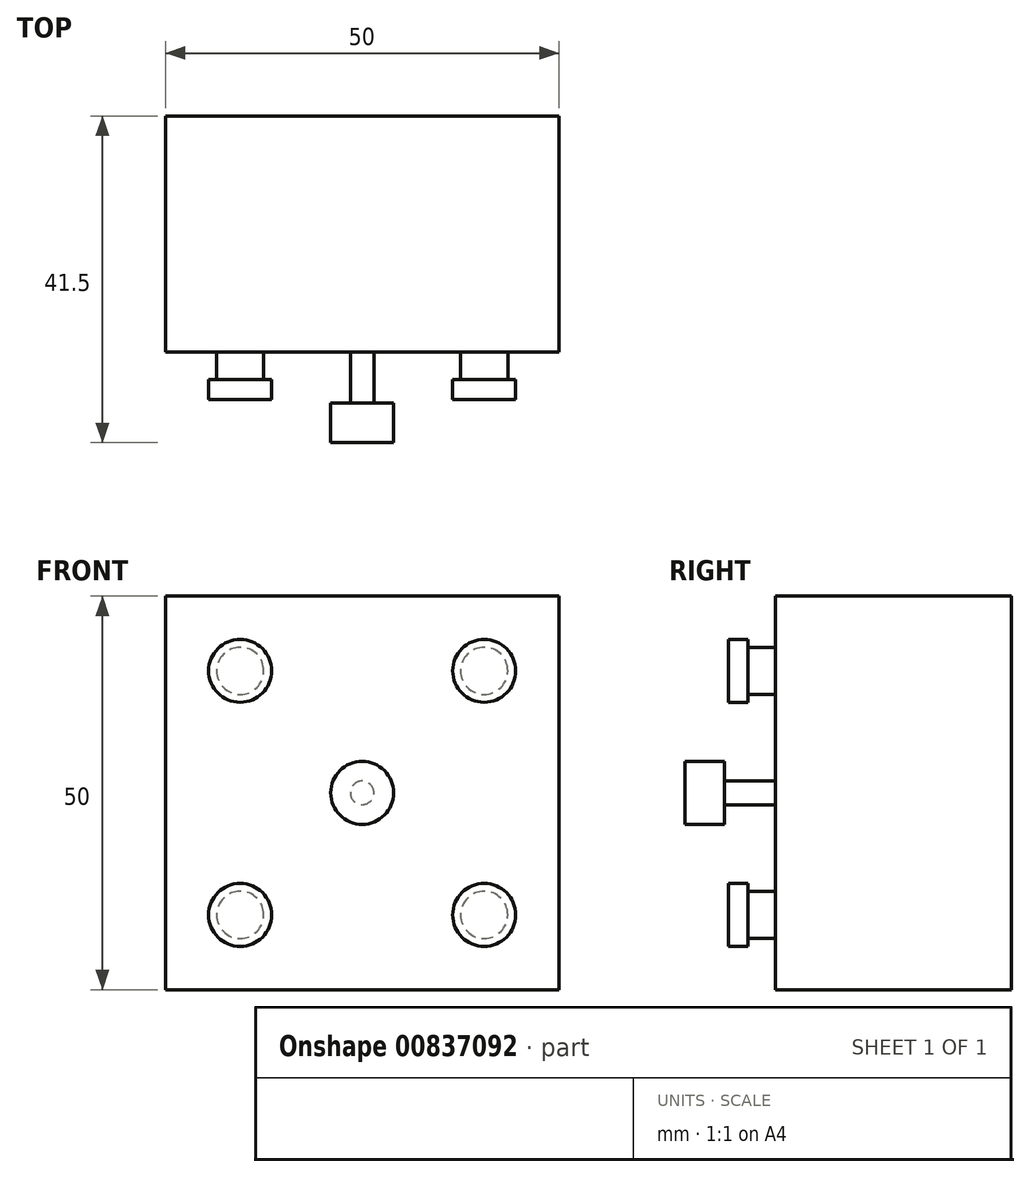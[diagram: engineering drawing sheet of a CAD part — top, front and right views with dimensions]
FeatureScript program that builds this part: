
annotation { "Feature Type Name" : "Feature", "Feature Type Description" : "" }
export const myFeature = defineFeature(function(context is Context, id is Id, definition is map)
    precondition{}
    {
        {
            var Q0;
            Q0=qCreatedBy(makeId("Front.planeOp"),FACE);
            var sketch = newSketch(context, id + "F0", { "sketchPlane" : qUnion([Q0])});
            skLineSegment(sketch, "E0.bottom", {"start": v(-25, 25) * mm, "end": v(25, 25) * mm});
            skLineSegment(sketch, "E0.top", {"start": v(-25, -25) * mm, "end": v(25, -25) * mm});
            skLineSegment(sketch, "E0.left", {"start": v(-25, 25) * mm, "end": v(-25, -25) * mm});
            skLineSegment(sketch, "E0.right", {"start": v(25, 25) * mm, "end": v(25, -25) * mm});
            skPoint(sketch, "E0.middle", {"position": v(0, 0) * mm});
            skCircle(sketch, "E1", {"center": v(-15.5, 15.5) * mm, "radius": 4 * mm});
            skCircle(sketch, "E2", {"center": v(15.5, 15.5) * mm, "radius": 4 * mm});
            skCircle(sketch, "E3", {"center": v(-15.5, -15.5) * mm, "radius": 4 * mm});
            skCircle(sketch, "E4", {"center": v(15.5, -15.5) * mm, "radius": 4 * mm});
            skCircle(sketch, "E5", {"center": v(-15.5, 15.5) * mm, "radius": 3 * mm});
            skCircle(sketch, "E6", {"center": v(15.5, 15.5) * mm, "radius": 3 * mm});
            skCircle(sketch, "E7", {"center": v(-15.5, -15.5) * mm, "radius": 3 * mm});
            skCircle(sketch, "E8", {"center": v(15.5, -15.5) * mm, "radius": 3 * mm});
            skLineSegment(sketch, "E9", {"start": v(25, 25) * mm, "end": v(-25, -25) * mm, "construction": true});
            skLineSegment(sketch, "E10", {"start": v(-25, 25) * mm, "end": v(25, -25) * mm, "construction": true});
            skCircle(sketch, "E11", {"center": v(0, 0) * mm, "radius": 4 * mm});
            skCircle(sketch, "E12", {"center": v(0, 0) * mm, "radius": 1.5 * mm});
            skSolve(sketch);
        }
        {
            var Q0;
            Q0=makeQuery(id+"F0.imprint","IMPRINT",FACE,{"disambiguationData":[TD([[makeQuery(id+"F0.imprint","IMPRINT",EDGE,{"derivedFrom":sQuery(id+"F0.wireOp",EDGE,"E0.bottom")}),-1.0]])]});
            var Q1;
            Q1=makeQuery(id+"F0.imprint","IMPRINT",FACE,{"disambiguationData":[TD([[makeQuery(id+"F0.imprint","IMPRINT",EDGE,{"derivedFrom":sQuery(id+"F0.wireOp",EDGE,"E1")}),1.0]])]});
            var Q2;
            Q2=makeQuery(id+"F0.imprint","IMPRINT",FACE,{"disambiguationData":[TD([[makeQuery(id+"F0.imprint","IMPRINT",EDGE,{"derivedFrom":sQuery(id+"F0.wireOp",EDGE,"E3")}),1.0]])]});
            var Q3;
            Q3=makeQuery(id+"F0.imprint","IMPRINT",FACE,{"disambiguationData":[TD([[makeQuery(id+"F0.imprint","IMPRINT",EDGE,{"derivedFrom":sQuery(id+"F0.wireOp",EDGE,"E4")}),1.0]])]});
            var Q4;
            Q4=makeQuery(id+"F0.imprint","IMPRINT",FACE,{"disambiguationData":[TD([[makeQuery(id+"F0.imprint","IMPRINT",EDGE,{"derivedFrom":sQuery(id+"F0.wireOp",EDGE,"E2")}),1.0]])]});
            var Q5;
            Q5=makeQuery(id+"F0.imprint","IMPRINT",FACE,{"disambiguationData":[TD([[makeQuery(id+"F0.imprint","IMPRINT",EDGE,{"derivedFrom":sQuery(id+"F0.wireOp",EDGE,"E8")}),1.0]])]});
            var Q6;
            Q6=makeQuery(id+"F0.imprint","IMPRINT",FACE,{"disambiguationData":[TD([[makeQuery(id+"F0.imprint","IMPRINT",EDGE,{"derivedFrom":sQuery(id+"F0.wireOp",EDGE,"E7")}),1.0]])]});
            var Q7;
            Q7=makeQuery(id+"F0.imprint","IMPRINT",FACE,{"disambiguationData":[TD([[makeQuery(id+"F0.imprint","IMPRINT",EDGE,{"derivedFrom":sQuery(id+"F0.wireOp",EDGE,"E6")}),1.0]])]});
            var Q8;
            Q8=makeQuery(id+"F0.imprint","IMPRINT",FACE,{"disambiguationData":[TD([[makeQuery(id+"F0.imprint","IMPRINT",EDGE,{"derivedFrom":sQuery(id+"F0.wireOp",EDGE,"E5")}),1.0]])]});
            var Q9;
            Q9=makeQuery(id+"F0.imprint","IMPRINT",FACE,{"disambiguationData":[TD([[makeQuery(id+"F0.imprint","IMPRINT",EDGE,{"derivedFrom":sQuery(id+"F0.wireOp",EDGE,"E11")}),1.0]])]});
            var Q10;
            Q10=makeQuery(id+"F0.imprint","IMPRINT",FACE,{"disambiguationData":[TD([[makeQuery(id+"F0.imprint","IMPRINT",EDGE,{"derivedFrom":sQuery(id+"F0.wireOp",EDGE,"E12")}),1.0]])]});
            extrude(context, id + "F1", {"entities" : qUnion([Q0, Q1, Q2, Q3, Q4, Q5, Q6, Q7, Q8, Q9, Q10]), "oppositeDirection" : true, "depth" : 30 * mm, "offsetDistance" : 25 * mm});
        }
        {
            var Q0;
            Q0=makeQuery(id+"F0.imprint","IMPRINT",FACE,{"disambiguationData":[TD([[makeQuery(id+"F0.imprint","IMPRINT",EDGE,{"derivedFrom":sQuery(id+"F0.wireOp",EDGE,"E1")}),1.0]])]});
            var Q1;
            Q1=makeQuery(id+"F0.imprint","IMPRINT",FACE,{"disambiguationData":[TD([[makeQuery(id+"F0.imprint","IMPRINT",EDGE,{"derivedFrom":sQuery(id+"F0.wireOp",EDGE,"E2")}),1.0]])]});
            var Q2;
            Q2=makeQuery(id+"F0.imprint","IMPRINT",FACE,{"disambiguationData":[TD([[makeQuery(id+"F0.imprint","IMPRINT",EDGE,{"derivedFrom":sQuery(id+"F0.wireOp",EDGE,"E4")}),1.0]])]});
            var Q3;
            Q3=makeQuery(id+"F0.imprint","IMPRINT",FACE,{"disambiguationData":[TD([[makeQuery(id+"F0.imprint","IMPRINT",EDGE,{"derivedFrom":sQuery(id+"F0.wireOp",EDGE,"E3")}),1.0]])]});
            extrude(context, id + "F2", {"entities" : qUnion([Q0, Q1, Q2, Q3]), "operationType" : NewBodyOperationType.ADD, "depth" : 6 * mm, "offsetDistance" : 25 * mm});
        }
        {
            var Q0;
            Q0=makeQuery(id+"F0.imprint","IMPRINT",FACE,{"disambiguationData":[TD([[makeQuery(id+"F0.imprint","IMPRINT",EDGE,{"derivedFrom":sQuery(id+"F0.wireOp",EDGE,"E5")}),1.0]])]});
            var Q1;
            Q1=makeQuery(id+"F0.imprint","IMPRINT",FACE,{"disambiguationData":[TD([[makeQuery(id+"F0.imprint","IMPRINT",EDGE,{"derivedFrom":sQuery(id+"F0.wireOp",EDGE,"E6")}),1.0]])]});
            var Q2;
            Q2=makeQuery(id+"F0.imprint","IMPRINT",FACE,{"disambiguationData":[TD([[makeQuery(id+"F0.imprint","IMPRINT",EDGE,{"derivedFrom":sQuery(id+"F0.wireOp",EDGE,"E8")}),1.0]])]});
            var Q3;
            Q3=makeQuery(id+"F0.imprint","IMPRINT",FACE,{"disambiguationData":[TD([[makeQuery(id+"F0.imprint","IMPRINT",EDGE,{"derivedFrom":sQuery(id+"F0.wireOp",EDGE,"E7")}),1.0]])]});
            extrude(context, id + "F3", {"entities" : qUnion([Q0, Q1, Q2, Q3]), "operationType" : NewBodyOperationType.ADD, "depth" : 6 * mm, "offsetDistance" : 25 * mm});
        }
        {
            var Q0;
            Q0=makeQuery(id+"F0.imprint","IMPRINT",FACE,{"disambiguationData":[TD([[makeQuery(id+"F0.imprint","IMPRINT",EDGE,{"derivedFrom":sQuery(id+"F0.wireOp",EDGE,"E11")}),1.0]])]});
            var Q1;
            Q1=makeQuery(id+"F0.imprint","IMPRINT",FACE,{"disambiguationData":[TD([[makeQuery(id+"F0.imprint","IMPRINT",EDGE,{"derivedFrom":sQuery(id+"F0.wireOp",EDGE,"E12")}),1.0]])]});
            extrude(context, id + "F4", {"entities" : qUnion([Q0, Q1]), "operationType" : NewBodyOperationType.ADD, "depth" : 11.5 * mm, "offsetDistance" : 25 * mm});
        }
        {
            var Q0;
            Q0=makeQuery(id+"F0.imprint","IMPRINT",FACE,{"disambiguationData":[TD([[makeQuery(id+"F0.imprint","IMPRINT",EDGE,{"derivedFrom":sQuery(id+"F0.wireOp",EDGE,"E3")}),1.0]])]});
            var Q1;
            Q1=makeQuery(id+"F0.imprint","IMPRINT",FACE,{"disambiguationData":[TD([[makeQuery(id+"F0.imprint","IMPRINT",EDGE,{"derivedFrom":sQuery(id+"F0.wireOp",EDGE,"E4")}),1.0]])]});
            var Q2;
            Q2=makeQuery(id+"F0.imprint","IMPRINT",FACE,{"disambiguationData":[TD([[makeQuery(id+"F0.imprint","IMPRINT",EDGE,{"derivedFrom":sQuery(id+"F0.wireOp",EDGE,"E2")}),1.0]])]});
            var Q3;
            Q3=makeQuery(id+"F0.imprint","IMPRINT",FACE,{"disambiguationData":[TD([[makeQuery(id+"F0.imprint","IMPRINT",EDGE,{"derivedFrom":sQuery(id+"F0.wireOp",EDGE,"E1")}),1.0]])]});
            extrude(context, id + "F5", {"entities" : qUnion([Q0, Q1, Q2, Q3]), "operationType" : NewBodyOperationType.REMOVE, "depth" : 3.5 * mm, "offsetDistance" : 25 * mm});
        }
        {
            var Q0;
            Q0=makeQuery(id+"F0.imprint","IMPRINT",FACE,{"disambiguationData":[TD([[makeQuery(id+"F0.imprint","IMPRINT",EDGE,{"derivedFrom":sQuery(id+"F0.wireOp",EDGE,"E11")}),1.0]])]});
            extrude(context, id + "F6", {"entities" : qUnion([Q0]), "operationType" : NewBodyOperationType.REMOVE, "depth" : 6.5 * mm, "offsetDistance" : 25 * mm});
        }
    });
